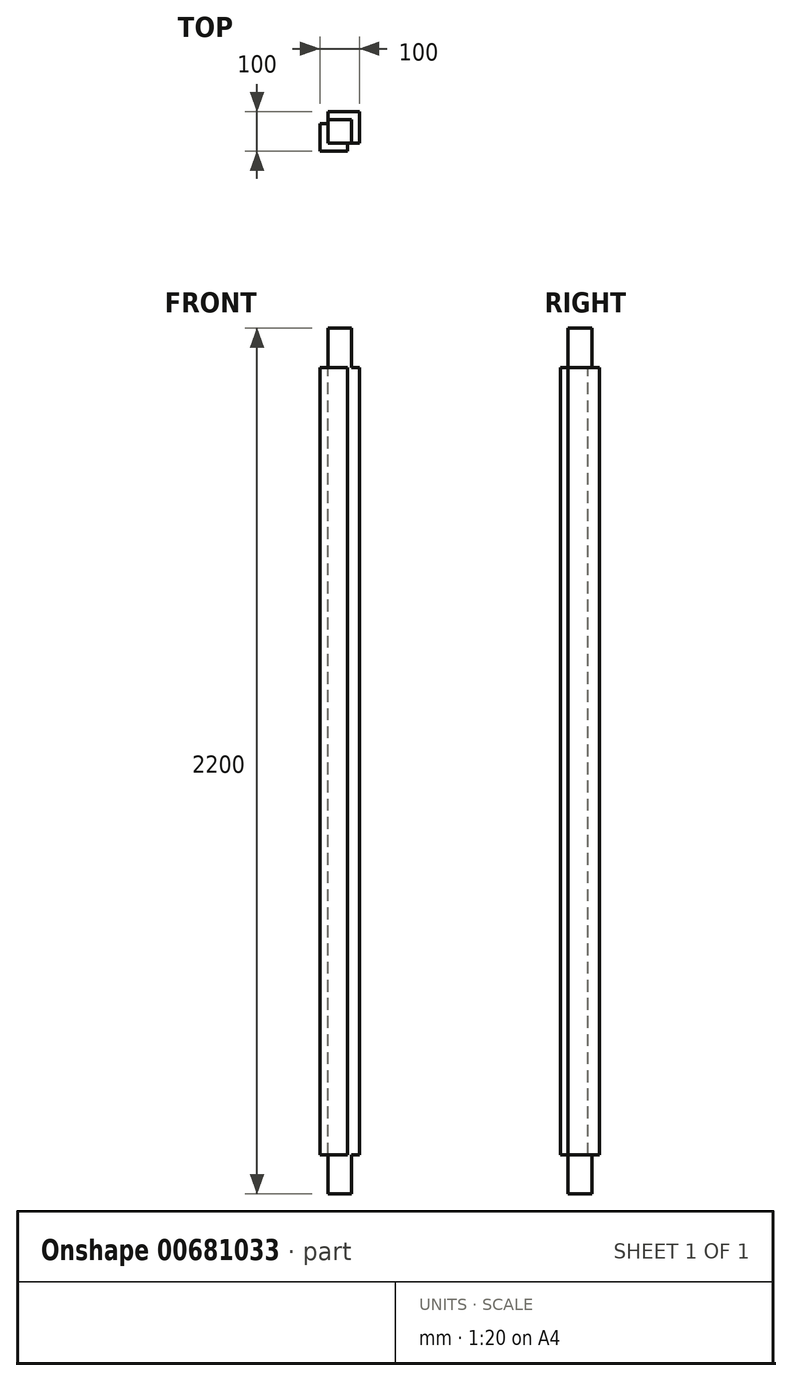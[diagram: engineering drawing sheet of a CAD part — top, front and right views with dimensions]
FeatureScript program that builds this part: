
annotation { "Feature Type Name" : "Feature", "Feature Type Description" : "" }
export const myFeature = defineFeature(function(context is Context, id is Id, definition is map)
    precondition{}
    {
        {
            var Q0;
            Q0=qCreatedBy(makeId("Front.planeOp"),FACE);
            var sketch = newSketch(context, id + "F0", { "sketchPlane" : qUnion([Q0])});
            skLineSegment(sketch, "E0.bottom", {"start": v(0, 0) * mm, "end": v(100, 0) * mm});
            skLineSegment(sketch, "E0.top", {"start": v(0, 2200) * mm, "end": v(100, 2200) * mm});
            skLineSegment(sketch, "E0.left", {"start": v(0, 0) * mm, "end": v(0, 2200) * mm});
            skLineSegment(sketch, "E0.right", {"start": v(100, 0) * mm, "end": v(100, 2200) * mm});
            skSolve(sketch);
        }
        {
            var Q0;
            Q0 = qSketchRegion(id + "F0", true);
            extrude(context, id + "F1", {"entities" : qUnion([Q0]), "depth" : 100 * mm, "offsetDistance" : 25 * mm});
        }
        {
            var Q0;
            Q0=makeQuery(id+"F1.opExtrude","CAP_FACE",FACE,{"disambiguationData":[OSD([sQuery(id+"F0.wireOp",EDGE,"E0.bottom"),sQuery(id+"F0.wireOp",EDGE,"E0.top"),sQuery(id+"F0.wireOp",EDGE,"E0.left"),sQuery(id+"F0.wireOp",EDGE,"E0.right")])],"isStart":false});
            var sketch = newSketch(context, id + "F2", { "sketchPlane" : qUnion([Q0])});
            skLineSegment(sketch, "E1.bottom", {"start": v(100, 0) * mm, "end": v(70, 0) * mm});
            skLineSegment(sketch, "E1.top", {"start": v(100, 2200) * mm, "end": v(70, 2200) * mm});
            skLineSegment(sketch, "E1.left", {"start": v(100, 0) * mm, "end": v(100, 2200) * mm});
            skLineSegment(sketch, "E1.right", {"start": v(70, 0) * mm, "end": v(70, 2200) * mm});
            skSolve(sketch);
        }
        {
            var Q0;
            Q0 = qSketchRegion(id + "F2", true);
            extrude(context, id + "F3", {"entities" : qUnion([Q0]), "operationType" : NewBodyOperationType.REMOVE, "oppositeDirection" : true, "depth" : 20 * mm, "offsetDistance" : 25 * mm});
        }
        {
            var Q0;
            Q0=makeQuery(id+"F1.opExtrude","SWEPT_FACE",FACE,{"disambiguationData":[OSD([sQuery(id+"F0.wireOp",EDGE,"E0.left")])]});
            var sketch = newSketch(context, id + "F4", { "sketchPlane" : qUnion([Q0])});
            skLineSegment(sketch, "E2.bottom", {"start": v(0, 0) * mm, "end": v(30, 0) * mm});
            skLineSegment(sketch, "E2.top", {"start": v(0, 2200) * mm, "end": v(30, 2200) * mm});
            skLineSegment(sketch, "E2.left", {"start": v(0, 0) * mm, "end": v(0, 2200) * mm});
            skLineSegment(sketch, "E2.right", {"start": v(30, 0) * mm, "end": v(30, 2200) * mm});
            skSolve(sketch);
        }
        {
            var Q0;
            Q0=makeQuery(id+"F4.imprint","IMPRINT",FACE,{"disambiguationData":[TD([[makeQuery(id+"F4.imprint","IMPRINT",EDGE,{"derivedFrom":sQuery(id+"F4.wireOp",EDGE,"E2.bottom")}),-1.0]])]});
            extrude(context, id + "F5", {"entities" : qUnion([Q0]), "operationType" : NewBodyOperationType.REMOVE, "oppositeDirection" : true, "depth" : 20 * mm, "offsetDistance" : 25 * mm});
        }
        {
            var Q0;
            Q0=makeQuery(id+"F1.opExtrude","SWEPT_FACE",FACE,{"disambiguationData":[OSD([sQuery(id+"F0.wireOp",EDGE,"E0.top")])]});
            var sketch = newSketch(context, id + "F6", { "sketchPlane" : qUnion([Q0])});
            skLineSegment(sketch, "E3.bottom", {"start": v(80, -20) * mm, "end": v(20, -20) * mm});
            skLineSegment(sketch, "E3.top", {"start": v(80, -80) * mm, "end": v(20, -80) * mm});
            skLineSegment(sketch, "E3.left", {"start": v(80, -20) * mm, "end": v(80, -80) * mm});
            skLineSegment(sketch, "E3.right", {"start": v(20, -20) * mm, "end": v(20, -80) * mm});
            skSolve(sketch);
        }
        {
            var Q0;
            {var subQ4=sQuery(id+"F6.wireOp",EDGE,"E3.bottom");Q0=makeQuery(id+"F6.imprint","IMPRINT",FACE,{"disambiguationData":[TD([[makeQuery(id+"F6.imprint","IMPRINT",EDGE,{"derivedFrom":subQ4}),-1.0]])]});}
            var Q1;
            {var subQ0=sQuery(id+"F0.wireOp",EDGE,"E0.top");Q1=makeQuery(id+"F6.imprint","IMPRINT",FACE,{"disambiguationData":[TD([[makeQuery(id+"F6.imprint","IMPRINT",EDGE,{"derivedFrom":makeQuery(id+"F1.opExtrude","CAP_EDGE",EDGE,{"disambiguationData":[OSD([subQ0])],"isStart":false})}),1.0]])]});}
            extrude(context, id + "F7", {"entities" : qUnion([Q0, Q1]), "operationType" : NewBodyOperationType.REMOVE, "oppositeDirection" : true, "depth" : 100 * mm, "offsetDistance" : 25 * mm});
        }
        {
            var Q0;
            Q0=makeQuery(id+"F1.opExtrude","SWEPT_FACE",FACE,{"disambiguationData":[OSD([sQuery(id+"F0.wireOp",EDGE,"E0.bottom")])]});
            var sketch = newSketch(context, id + "F8", { "sketchPlane" : qUnion([Q0])});
            skLineSegment(sketch, "E4.bottom", {"start": v(20, 20) * mm, "end": v(80, 20) * mm});
            skLineSegment(sketch, "E4.top", {"start": v(20, 80) * mm, "end": v(80, 80) * mm});
            skLineSegment(sketch, "E4.left", {"start": v(20, 20) * mm, "end": v(20, 80) * mm});
            skLineSegment(sketch, "E4.right", {"start": v(80, 20) * mm, "end": v(80, 80) * mm});
            skSolve(sketch);
        }
        {
            var Q0;
            {var subQ0=sQuery(id+"F0.wireOp",EDGE,"E0.bottom");Q0=makeQuery(id+"F8.imprint","IMPRINT",FACE,{"disambiguationData":[TD([[makeQuery(id+"F8.imprint","IMPRINT",EDGE,{"derivedFrom":makeQuery(id+"F1.opExtrude","CAP_EDGE",EDGE,{"disambiguationData":[OSD([subQ0])],"isStart":false})}),-1.0]])]});}
            var Q1;
            {var subQ4=sQuery(id+"F8.wireOp",EDGE,"E4.bottom");Q1=makeQuery(id+"F8.imprint","IMPRINT",FACE,{"disambiguationData":[TD([[makeQuery(id+"F8.imprint","IMPRINT",EDGE,{"derivedFrom":subQ4}),-1.0]])]});}
            extrude(context, id + "F9", {"entities" : qUnion([Q0, Q1]), "operationType" : NewBodyOperationType.REMOVE, "oppositeDirection" : true, "depth" : 100 * mm, "offsetDistance" : 25 * mm});
        }
    });
